# Revit family: 210_ef8d5d3433f04e83a89b3581a023a1
name_source: partatom
category: Mechanical Equipment
revit_build: Autodesk Revit 2018 (Build: 20170223_1515(x64)
units: mm (PartAtom-declared; Revit-internal decimal feet)

## family parameters
Always vertical = Yes
Classification = None
Cut with Voids When Loaded = No
Part Type = Breaks Into
Room Calculation Point = No
Round Connector Dimension = Use Diameter
Shared = No
Work Plane-Based = No

## types (12) — shared parameters
Description = Roof fan DVA AC
Manufacturer = Flexit
QmdConnectorList = 201;D;201;D
SW2 = No
URL = www.flexit.no
W = 500 mm
magiPartTypeId = 210
magiProductFamilyId = ef8d5d3433f04e83a89b3581a023a1

## per-type parameters (varying)
| type | D | L | X1 | X2 | X3 | Y1 | Y2 | Y3 | Z1 | Z2 | Z3 | Z4 | Z5 | magiProductId |
| 250-114660 | 250 mm | 437 mm | 197 mm | 271 mm | 243 mm | 81 mm | 112 mm | 101 mm | 25 mm  [stored 0.082021 ft] | 62 mm | 12 mm  [stored 0.0393701 ft] | 10 mm  [stored 0.0328084 ft] | 139 mm | f6d2f43a5c584203b289794301b0ce |
| 250-114661 | 250 mm | 437 mm | 197 mm | 271 mm | 243 mm | 81 mm | 112 mm | 101 mm | 25 mm  [stored 0.082021 ft] | 62 mm | 12 mm  [stored 0.0393701 ft] | 10 mm  [stored 0.0328084 ft] | 139 mm | a072dc485ce6451a867897369b7ff8 |
| 400-114662 | 400 mm | 598 mm | 269 mm | 373 mm | 335 mm | 111 mm | 154 mm | 139 mm | 33 mm | 83 mm | 17 mm | 13 mm | 186 mm | 7a08abf990f44d4fa79ea7963c73e1 |
| 400-114663 | 400 mm | 598 mm | 269 mm | 373 mm | 335 mm | 111 mm | 154 mm | 139 mm | 33 mm | 83 mm | 17 mm | 13 mm | 186 mm | 768a0650599d4ec2a406f82fbd0473 |
| 400-114664 | 400 mm | 670 mm | 302 mm | 430 mm | 387 mm | 125 mm | 178 mm | 160 mm  [stored 0.524934 ft] | 42 mm | 105 mm | 21 mm | 17 mm | 234 mm | b6c8f794a7324de2adfb6ff4014219 |
| 400-114665 | 400 mm | 670 mm | 302 mm | 430 mm | 387 mm | 125 mm | 178 mm | 160 mm  [stored 0.524934 ft] | 42 mm | 105 mm | 21 mm | 17 mm | 234 mm | d6337de7b76447d0bc95230f9a8f6d |
| 560-114666 | 560 mm | 931 mm | 419 mm | 583 mm | 524 mm | 174 mm | 241 mm | 217 mm | 52 mm  [stored 0.170604 ft] | 130 mm | 26 mm | 21 mm | 292 mm | 9e3dc2dc6c6449e5b4aaa991cd0c96 |
| 180-114655 | 180 mm | 337 mm | 152 mm | 194 mm  [stored 0.636483 ft] | 175 mm | 63 mm | 80 mm | 72 mm | 19 mm  [stored 0.062336 ft] | 48 mm | 10 mm  [stored 0.0328084 ft] | 8 mm  [stored 0.0262467 ft] | 106 mm | ff208c8bc37744e196a814951fd2ff |
| 180-114656 | 180 mm | 337 mm | 152 mm | 194 mm  [stored 0.636483 ft] | 175 mm | 63 mm | 80 mm | 72 mm | 19 mm  [stored 0.062336 ft] | 48 mm | 10 mm  [stored 0.0328084 ft] | 8 mm  [stored 0.0262467 ft] | 106 mm | 73a643e9a36a49e08f69249767a2d3 |
| 180-114657 | 180 mm | 337 mm | 152 mm | 194 mm  [stored 0.636483 ft] | 175 mm | 63 mm | 80 mm | 72 mm | 19 mm  [stored 0.062336 ft] | 48 mm | 10 mm  [stored 0.0328084 ft] | 8 mm  [stored 0.0262467 ft] | 106 mm | 42596d251d9d4da5a37b9589392578 |
| 180-114658 | 180 mm | 337 mm | 152 mm | 194 mm  [stored 0.636483 ft] | 175 mm | 63 mm | 80 mm | 72 mm | 19 mm  [stored 0.062336 ft] | 48 mm | 10 mm  [stored 0.0328084 ft] | 8 mm  [stored 0.0262467 ft] | 106 mm | ee92ef0b11d14d618a0095da64b03d |
| 180-114659 | 180 mm | 337 mm | 152 mm | 194 mm  [stored 0.636483 ft] | 175 mm | 63 mm | 80 mm | 72 mm | 19 mm  [stored 0.062336 ft] | 48 mm | 10 mm  [stored 0.0328084 ft] | 8 mm  [stored 0.0262467 ft] | 106 mm | f9b4416d534b4871a8fed9b6758c84 |

note: column(s) folded — value = type name in every type: MC Product Code

note: [stored X ft] marks values corroborated as IEEE doubles in the binary element streams (Revit-internal decimal feet)

## geometry (parser evidence)
native form markers: Sweep x1
no freeform markers — native parametric forms only
